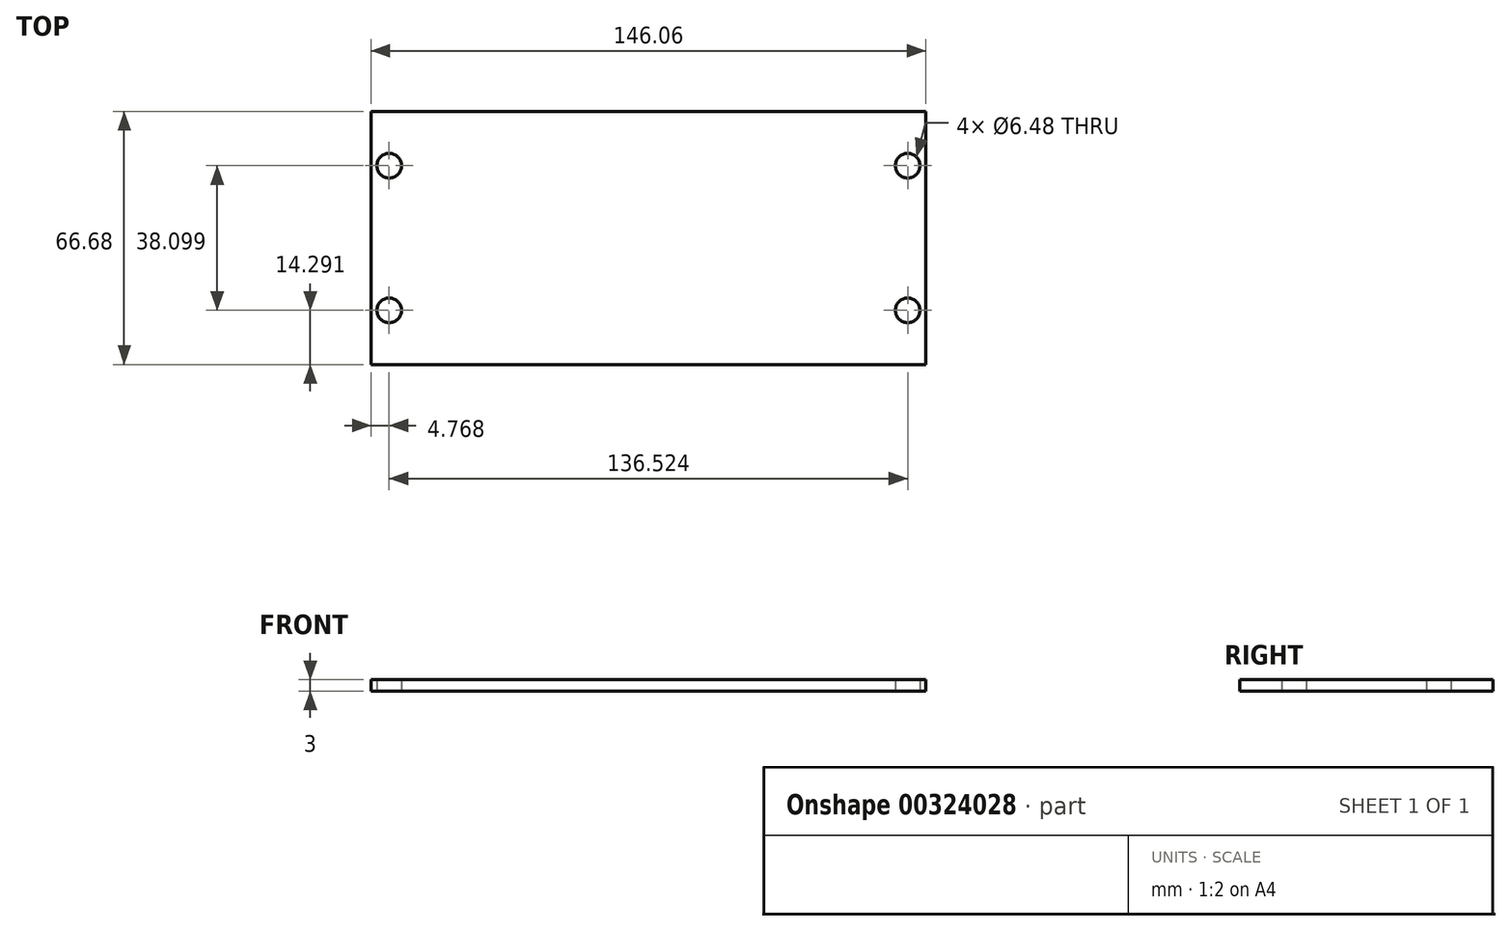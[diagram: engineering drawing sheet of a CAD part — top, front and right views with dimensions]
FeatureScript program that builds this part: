
annotation { "Feature Type Name" : "Feature", "Feature Type Description" : "" }
export const myFeature = defineFeature(function(context is Context, id is Id, definition is map)
    precondition{}
    {
        {
            var Q0;
            Q0=qCreatedBy(makeId("Top.planeOp"),FACE);
            var sketch = newSketch(context, id + "F0", { "sketchPlane" : qUnion([Q0])});
            skLineSegment(sketch, "E0", {"start": v(-68.26, 12.7) * mm, "end": v(-72.23, 12.7) * mm});
            skArc(sketch, "E1", {"start": v(-68.26, -25.4) * mm, "mid": v(-61.91, -19.05) * mm, "end": v(-68.26, -12.7) * mm});
            skArc(sketch, "E2", {"start": v(68.26, -12.7) * mm, "mid": v(61.91, -19.05) * mm, "end": v(68.26, -25.4) * mm});
            skLineSegment(sketch, "E3", {"start": v(72.22, -32.54) * mm, "end": v(72.22, -25.4) * mm});
            skLineSegment(sketch, "E4", {"start": v(-72.23, -32.54) * mm, "end": v(-72.23, -25.4) * mm});
            skLineSegment(sketch, "E5", {"start": v(72.22, -32.54) * mm, "end": v(-72.23, -32.54) * mm});
            skArc(sketch, "E6", {"start": v(68.26, 25.4) * mm, "mid": v(61.91, 19.05) * mm, "end": v(68.26, 12.7) * mm});
            skLineSegment(sketch, "E7", {"start": v(-72.23, 32.54) * mm, "end": v(72.23, 32.54) * mm});
            skLineSegment(sketch, "E8", {"start": v(68.26, 12.7) * mm, "end": v(72.22, 12.7) * mm});
            skLineSegment(sketch, "E9", {"start": v(72.22, 25.4) * mm, "end": v(72.22, 32.54) * mm});
            skLineSegment(sketch, "E10", {"start": v(68.26, 25.4) * mm, "end": v(72.22, 25.4) * mm});
            skLineSegment(sketch, "E11", {"start": v(72.22, -12.7) * mm, "end": v(72.22, 12.7) * mm});
            skLineSegment(sketch, "E12", {"start": v(68.26, -12.7) * mm, "end": v(72.22, -12.7) * mm});
            skLineSegment(sketch, "E13", {"start": v(-68.26, -12.7) * mm, "end": v(-72.23, -12.7) * mm});
            skLineSegment(sketch, "E14", {"start": v(-68.26, -25.4) * mm, "end": v(-72.23, -25.4) * mm});
            skLineSegment(sketch, "E15", {"start": v(68.26, -25.4) * mm, "end": v(72.22, -25.4) * mm});
            skLineSegment(sketch, "E16", {"start": v(-72.23, -12.7) * mm, "end": v(-72.23, 12.7) * mm});
            skArc(sketch, "E17", {"start": v(-68.26, 12.7) * mm, "mid": v(-61.91, 19.05) * mm, "end": v(-68.26, 25.4) * mm});
            skLineSegment(sketch, "E18", {"start": v(-72.23, 25.4) * mm, "end": v(-72.23, 32.54) * mm});
            skLineSegment(sketch, "E19", {"start": v(-68.26, 25.4) * mm, "end": v(-72.23, 25.4) * mm});
            skCircle(sketch, "E20", {"center": v(68.26, 19.05) * mm, "radius": 3.24 * mm});
            skCircle(sketch, "E21", {"center": v(68.26, -19.05) * mm, "radius": 3.24 * mm});
            skLineSegment(sketch, "E22", {"start": v(73.03, -33.34) * mm, "end": v(73.03, 33.34) * mm});
            skLineSegment(sketch, "E23", {"start": v(-73.03, 33.34) * mm, "end": v(73.03, 33.34) * mm});
            skLineSegment(sketch, "E24", {"start": v(-73.03, -33.34) * mm, "end": v(-73.03, 33.34) * mm});
            skLineSegment(sketch, "E25", {"start": v(73.03, -33.34) * mm, "end": v(-73.03, -33.34) * mm});
            skCircle(sketch, "E26", {"center": v(-68.26, -19.05) * mm, "radius": 3.24 * mm});
            skCircle(sketch, "E27", {"center": v(-68.26, 19.05) * mm, "radius": 3.24 * mm});
            skSolve(sketch);
        }
        {
            var Q0;
            Q0 = qSketchRegion(id + "F0", true);
            var Q1;
            Q1=makeQuery(id+"F0.imprint","IMPRINT",FACE,{"disambiguationData":[TD([[makeQuery(id+"F0.imprint","IMPRINT",EDGE,{"derivedFrom":sQuery(id+"F0.wireOp",EDGE,"E12")}),1.0]])]});
            extrude(context, id + "F1", {"entities" : qUnion([Q0, Q1]), "depth" : 3 * mm});
        }
    });
